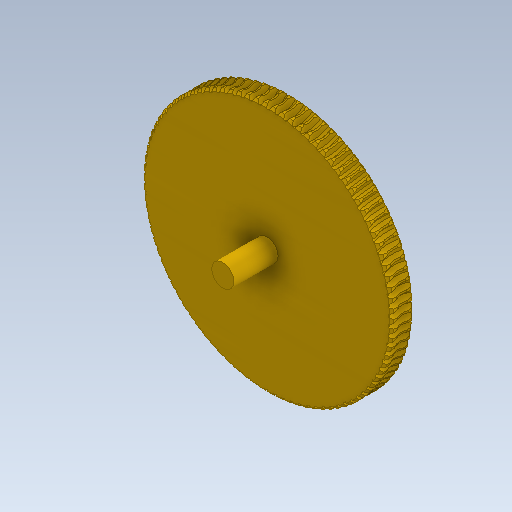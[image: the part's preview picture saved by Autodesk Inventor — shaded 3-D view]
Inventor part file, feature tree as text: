
AUTODESK INVENTOR PART (.ipt)
format: ipt  version: 2020.3 (Build 243373000, 373)  size: 1,772,544 bytes
history: native  units: mm (DEFAULTED — no unit token found)
features: other x8, sketch x4, plane x3, extrude x2, pattern_circular x1
ambient origin geometry x5: Origin, X Axis, Y Axis, Z Axis, Center Point
bodies: Solid1 (feature_tree)
feature tree (18):
  other  "Tooth Plane"
  other  "Base Body Sketch"
  other  "Base Body"
  other  "Base Body2"
  plane  "Work Plane13"
  other  "Tooth"
  pattern_circular  "Tooth Pattern"  [2 undecoded]
  plane  "Work Plane14"
  plane  "Work Plane15"
  extrude  "Extrusion2"  Depth=7.680818mm
  sketch  "Sketch11"  dims[d38=76.808176mm]
  extrude  "Extrusion3"  Depth=6.35mm
  other  "Tooth Sketch"
  sketch  "Sketch8"  dims[d35=90.0deg]
  other  "Srf1"
  sketch  "Sketch10"  dims[d37=-0.996687mm]
  sketch  "Sketch12"  dims[d39=3.490659mm d40=5.837421mm d41=7.680818mm d42=1.4478mm d43=90.0deg d44=900.0mm d46=360.0deg d50=7.600335mm d68=76.808176mm d69=0.0mm d73=0.0mm d75=0.349066mm d77=138.254716mm d78=12.7mm d79=0.0mm d80=0.0mm d81=0.0mm d82=0.0mm d83=0.349066mm d84=0.0mm d85=180.0deg d86=76.808176mm d87=142.863207mm d89=12.289308mm d90=90.0deg d92=12.7mm d93=76.808176mm d97=12.7mm d98=25.4mm d99=0.0mm d100=6.35mm d101=6.35mm d102=0.0mm]
  other  "Pitch Diameter"
note: 2 required parameter values undecoded (feature->parameter linkage not recoverable at this tier; creation-order binding heuristic only, values carry confidence <= 0.55)
